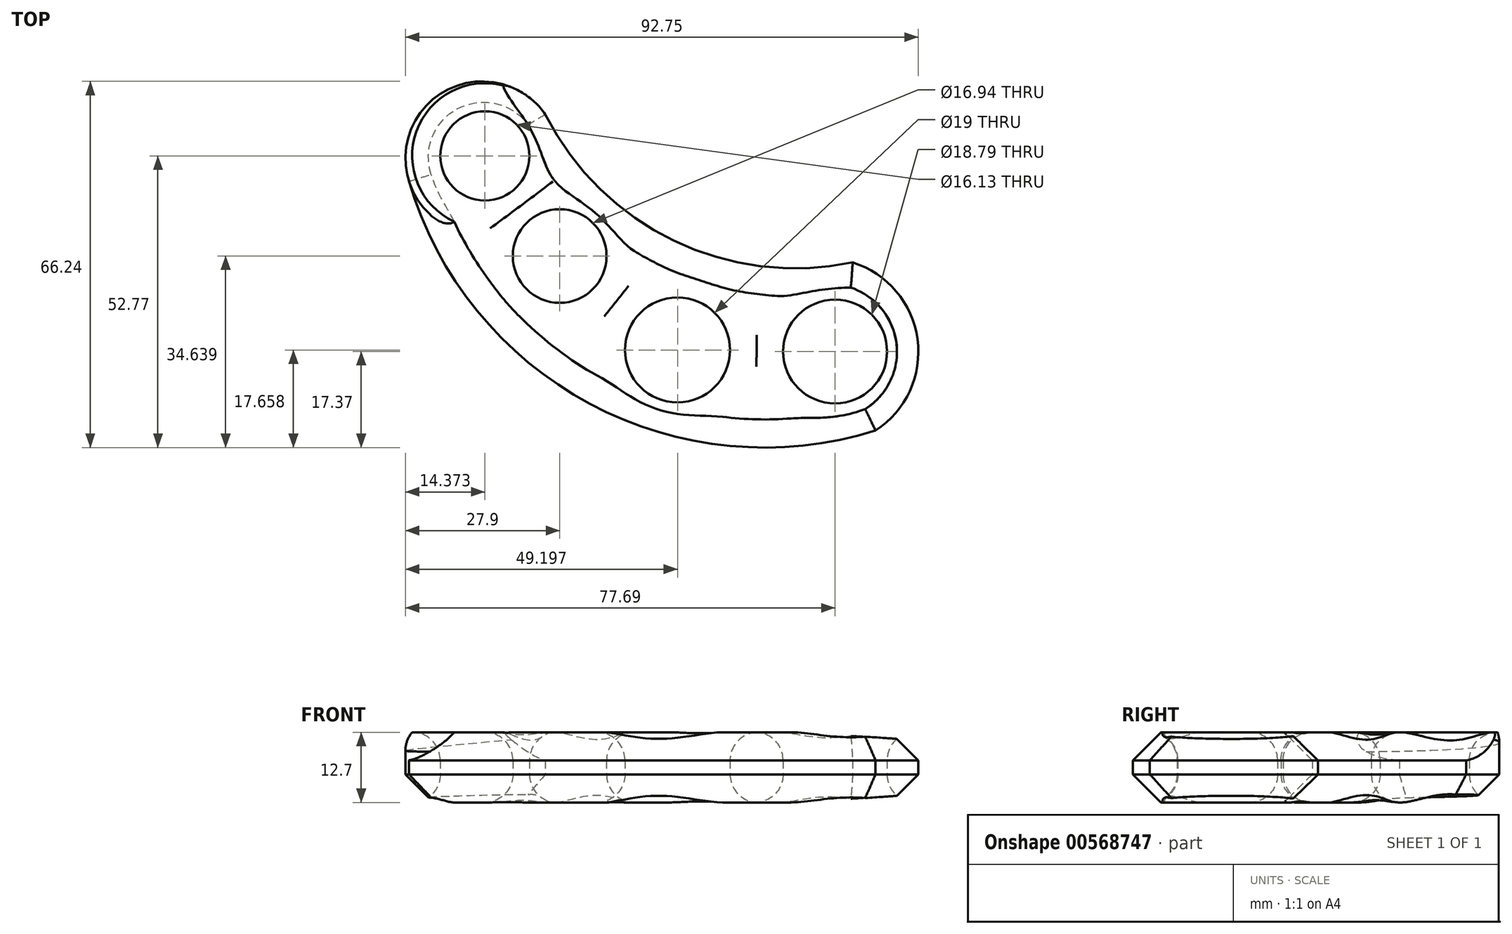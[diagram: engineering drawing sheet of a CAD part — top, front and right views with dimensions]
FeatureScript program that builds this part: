
annotation { "Feature Type Name" : "Feature", "Feature Type Description" : "" }
export const myFeature = defineFeature(function(context is Context, id is Id, definition is map)
    precondition{}
    {
        {
            var Q0;
            Q0=qCreatedBy(makeId("Top.planeOp"),FACE);
            var sketch = newSketch(context, id + "F0", { "sketchPlane" : qUnion([Q0])});
            skCircle(sketch, "E0", {"center": v(-26.2, 19.86) * mm, "radius": 8.47 * mm});
            skCircle(sketch, "E1", {"center": v(-4.9, 2.88) * mm, "radius": 9.5 * mm});
            skCircle(sketch, "E2", {"center": v(23.6, 2.6) * mm, "radius": 9.4 * mm});
            skCircle(sketch, "E3", {"center": v(-39.72, 38) * mm, "radius": 8.06 * mm});
            skArc(sketch, "E4", {"start": v(-28.78, 45.47) * mm, "mid": v(-5.56, 22.64) * mm, "end": v(26.77, 18.7) * mm});
            skArc(sketch, "E5", {"start": v(-53.45, 33.39) * mm, "mid": v(-20.73, -6.85) * mm, "end": v(30.9, -11.72) * mm});
            skArc(sketch, "E6", {"start": v(-28.78, 45.47) * mm, "mid": v(-46.31, 50.04) * mm, "end": v(-53.45, 33.39) * mm});
            skArc(sketch, "E7", {"start": v(30.9, -11.72) * mm, "mid": v(38.5, 4.8) * mm, "end": v(26.77, 18.7) * mm});
            skSolve(sketch);
        }
        {
            var Q0;
            Q0 = qSketchRegion(id + "F0", true);
            extrude(context, id + "F1", {"entities" : qUnion([Q0]), "depth" : 12.7 * mm, "offsetDistance" : 25.4 * mm});
        }
        {
            var Q0;
            Q0=makeQuery(id+"F1.opExtrude","CAP_EDGE",EDGE,{"disambiguationData":[OSD([sQuery(id+"F0.wireOp",EDGE,"E0")])],"isStart":false});
            var Q1;
            Q1=makeQuery(id+"F1.opExtrude","CAP_EDGE",EDGE,{"disambiguationData":[OSD([sQuery(id+"F0.wireOp",EDGE,"E3")])],"isStart":false});
            var Q2;
            Q2=makeQuery(id+"F1.opExtrude","CAP_EDGE",EDGE,{"disambiguationData":[OSD([sQuery(id+"F0.wireOp",EDGE,"E1")])],"isStart":false});
            var Q3;
            Q3=makeQuery(id+"F1.opExtrude","CAP_EDGE",EDGE,{"disambiguationData":[OSD([sQuery(id+"F0.wireOp",EDGE,"E2")])],"isStart":false});
            fillet(context, id + "F2", {"entities" : qUnion([Q0, Q1, Q2, Q3]), "radius" : 5.08 * mm, "tangentPropagation" : true, "allowEdgeOverflow" : false});
        }
        {
            var Q0;
            Q0=makeQuery(id+"F1.opExtrude","CAP_EDGE",EDGE,{"disambiguationData":[OSD([sQuery(id+"F0.wireOp",EDGE,"E3")])],"isStart":true});
            var Q1;
            Q1=makeQuery(id+"F1.opExtrude","CAP_EDGE",EDGE,{"disambiguationData":[OSD([sQuery(id+"F0.wireOp",EDGE,"E0")])],"isStart":true});
            var Q2;
            Q2=makeQuery(id+"F1.opExtrude","CAP_EDGE",EDGE,{"disambiguationData":[OSD([sQuery(id+"F0.wireOp",EDGE,"E1")])],"isStart":true});
            var Q3;
            Q3=makeQuery(id+"F1.opExtrude","CAP_EDGE",EDGE,{"disambiguationData":[OSD([sQuery(id+"F0.wireOp",EDGE,"E2")])],"isStart":true});
            fillet(context, id + "F3", {"entities" : qUnion([Q0, Q1, Q2, Q3]), "radius" : 5.08 * mm, "tangentPropagation" : true, "allowEdgeOverflow" : false});
        }
        {
            var Q0;
            Q0=makeQuery(id+"F1.opExtrude","CAP_EDGE",EDGE,{"disambiguationData":[OSD([sQuery(id+"F0.wireOp",EDGE,"E5")])],"isStart":true});
            var Q1;
            Q1=makeQuery(id+"F1.opExtrude","CAP_EDGE",EDGE,{"disambiguationData":[OSD([sQuery(id+"F0.wireOp",EDGE,"E4")])],"isStart":true});
            var Q2;
            Q2=makeQuery(id+"F1.opExtrude","CAP_EDGE",EDGE,{"disambiguationData":[OSD([sQuery(id+"F0.wireOp",EDGE,"E6")])],"isStart":true});
            var Q3;
            Q3=makeQuery(id+"F1.opExtrude","CAP_EDGE",EDGE,{"disambiguationData":[OSD([sQuery(id+"F0.wireOp",EDGE,"E7")])],"isStart":true});
            chamfer(context, id + "F4", {"entities" : qUnion([Q0, Q1, Q2, Q3]), "width" : 5.08 * mm, "tangentPropagation" : true});
        }
        {
            var Q0;
            Q0=makeQuery(id+"F1.opExtrude","CAP_EDGE",EDGE,{"disambiguationData":[OSD([sQuery(id+"F0.wireOp",EDGE,"E5")])],"isStart":false});
            var Q1;
            Q1=makeQuery(id+"F1.opExtrude","CAP_EDGE",EDGE,{"disambiguationData":[OSD([sQuery(id+"F0.wireOp",EDGE,"E4")])],"isStart":false});
            chamfer(context, id + "F5", {"entities" : qUnion([Q0, Q1]), "width" : 5.08 * mm, "tangentPropagation" : true});
        }
        {
            var Q0;
            Q0=makeQuery(id+"F1.opExtrude","CAP_EDGE",EDGE,{"disambiguationData":[OSD([sQuery(id+"F0.wireOp",EDGE,"E6")])],"isStart":false});
            fillet(context, id + "F6", {"entities" : qUnion([Q0]), "radius" : 5.08 * mm, "tangentPropagation" : true, "allowEdgeOverflow" : false});
        }
        {
            var Q0;
            Q0=makeQuery(id+"F1.opExtrude","CAP_EDGE",EDGE,{"disambiguationData":[OSD([sQuery(id+"F0.wireOp",EDGE,"E7")])],"isStart":false});
            chamfer(context, id + "F7", {"entities" : qUnion([Q0]), "width" : 5.08 * mm, "tangentPropagation" : true});
        }
    });
